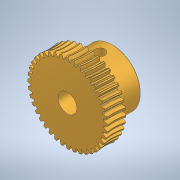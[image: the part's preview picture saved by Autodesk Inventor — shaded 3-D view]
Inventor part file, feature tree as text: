
AUTODESK INVENTOR PART (.ipt)
format: ipt  version: 2022 (Build 260153000, 153)  size: 2,094,592 bytes
history: mixed  units: in
note: dims shown in document units (in); Inventor stores cm internally (conversion verified against a paired STEP export)
features: hole x1, sketch x1, imported_body x1
ambient origin geometry x8: Origin, YZ Plane, XZ Plane, XY Plane, X Axis, Y Axis, Z Axis, Center Point
bodies: Solid1 (imported_parasolid), Body1 (imported_parasolid)
feature tree (3):
  hole  "Hole1"  [1 undecoded]
  sketch  "Sketch1"  dims[d0=0.1969in d1=0.2362in d2=0.1575in d3=0.0787in d4=90.0deg d5=0.315in d6=0.8108in]
  imported_body  NMx_Import_Brep_tag  [imported B-rep: ~5 faces, bbox_mm=None]
note: 1 required parameter value undecoded (feature->parameter linkage not recoverable at this tier; creation-order binding heuristic only, values carry confidence <= 0.55)
